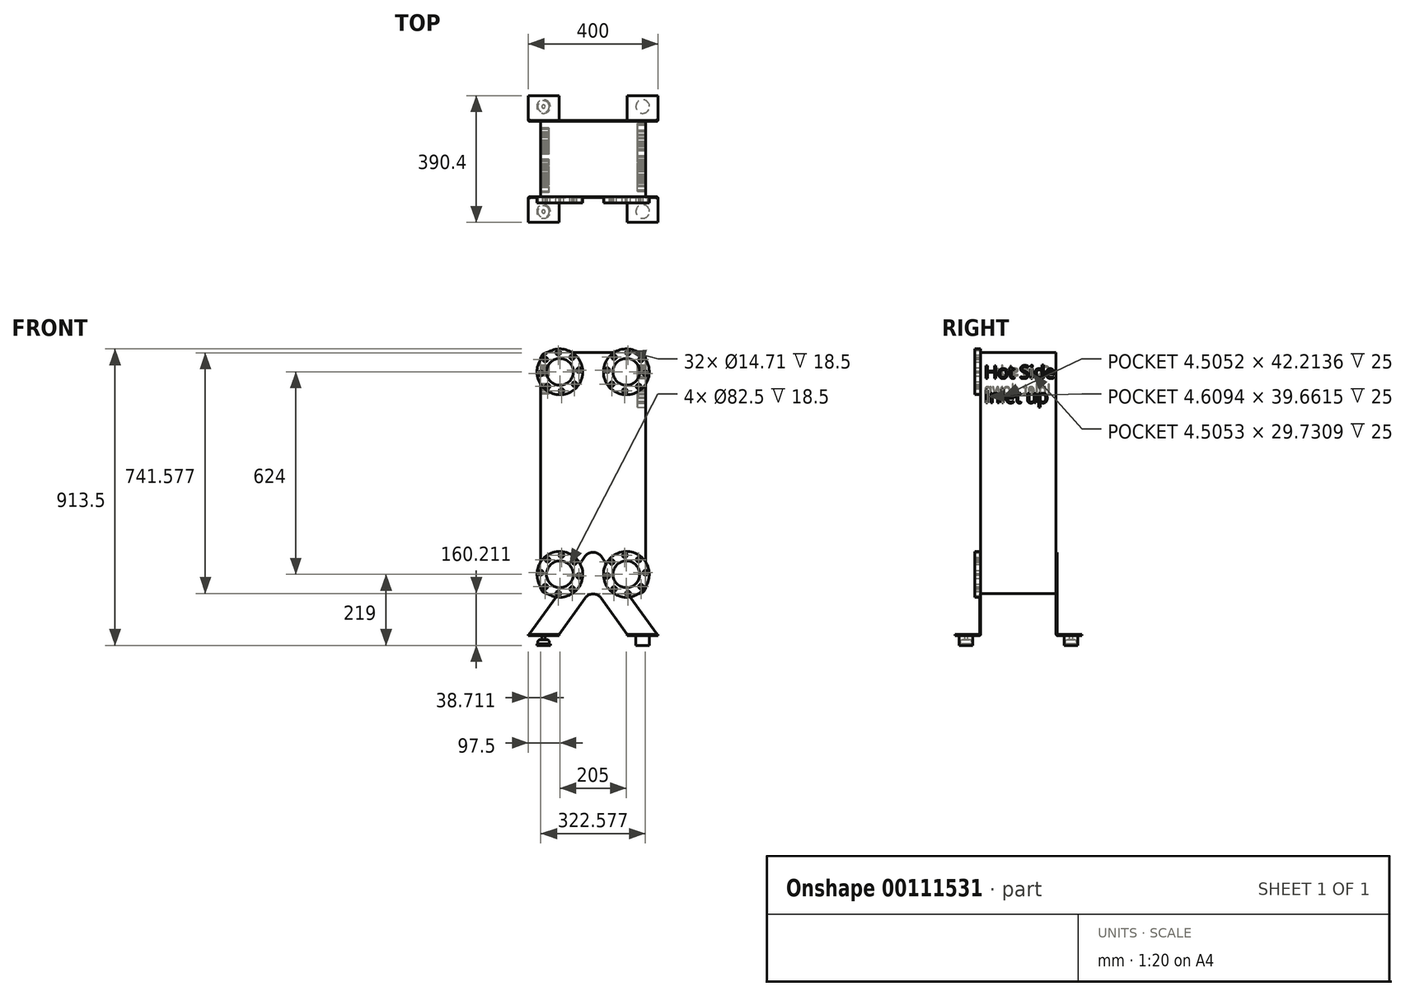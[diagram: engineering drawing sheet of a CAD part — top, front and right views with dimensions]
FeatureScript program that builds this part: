
annotation { "Feature Type Name" : "Feature", "Feature Type Description" : "" }
export const myFeature = defineFeature(function(context is Context, id is Id, definition is map)
    precondition{}
    {
        {
            var Q0;
            Q0=qCreatedBy(makeId("Front.planeOp"),FACE);
            var sketch = newSketch(context, id + "F0", { "sketchPlane" : qUnion([Q0])});
            skLineSegment(sketch, "E0.bottom", {"start": v(20, 0) * mm, "end": v(304, 0) * mm});
            skLineSegment(sketch, "E0.top", {"start": v(20, 742) * mm, "end": v(304, 742) * mm});
            skLineSegment(sketch, "E0.left", {"start": v(0, 20) * mm, "end": v(0, 722) * mm});
            skLineSegment(sketch, "E0.right", {"start": v(324, 20) * mm, "end": v(324, 722) * mm});
            skPoint(sketch, "E1", {"position": v(59.5, 683) * mm});
            skPoint(sketch, "E2", {"position": v(264.5, 683) * mm});
            skPoint(sketch, "E3", {"position": v(59.5, 59) * mm});
            skPoint(sketch, "E4", {"position": v(264.5, 59) * mm});
            skPoint(sketch, "E5", {"position": v(162, 0) * mm});
            skPoint(sketch, "E6", {"position": v(324, 371) * mm});
            skLineSegment(sketch, "E7", {"start": v(162, -155.7) * mm, "end": v(162, 967.26) * mm, "construction": true});
            skLineSegment(sketch, "E8", {"start": v(459.95, 371) * mm, "end": v(-440.95, 371) * mm, "construction": true});
            skLineSegment(sketch, "E9", {"start": v(59.5, 683) * mm, "end": v(162, 683) * mm});
            skLineSegment(sketch, "E10", {"start": v(162, 683) * mm, "end": v(264.5, 683) * mm});
            skLineSegment(sketch, "E11", {"start": v(59.5, 683) * mm, "end": v(59.5, 371) * mm});
            skLineSegment(sketch, "E12", {"start": v(59.5, 371) * mm, "end": v(59.5, 59) * mm});
            skPoint(sketch, "E13.visualSharp", {"position": v(0, 742) * mm});
            skArc(sketch, "E13.filletArc", {"start": v(20, 742) * mm, "mid": v(5.86, 736.14) * mm, "end": v(0, 722) * mm});
            skPoint(sketch, "E14.visualSharp", {"position": v(324, 742) * mm});
            skArc(sketch, "E14.filletArc", {"start": v(324, 722) * mm, "mid": v(318.14, 736.14) * mm, "end": v(304, 742) * mm});
            skPoint(sketch, "E15.visualSharp", {"position": v(324, 0) * mm});
            skArc(sketch, "E15.filletArc", {"start": v(304, 0) * mm, "mid": v(318.14, 5.86) * mm, "end": v(324, 20) * mm});
            skPoint(sketch, "E16.visualSharp", {"position": v(0, 0) * mm});
            skArc(sketch, "E16.filletArc", {"start": v(0, 20) * mm, "mid": v(5.86, 5.86) * mm, "end": v(20, 0) * mm});
            skSolve(sketch);
        }
        {
            var Q0;
            Q0=qSketchRegion(id+"F0",true);
            extrude(context, id + "F1", {"entities" : qUnion([Q0]), "oppositeDirection" : true, "depth" : 232.4 * mm});
        }
        {
            var Q0;
            Q0=makeQuery(id+"F0.imprint","IMPRINT",FACE,{"disambiguationData":[TD([[makeQuery(id+"F0.imprint","IMPRINT",EDGE,{"derivedFrom":sQuery(id+"F0.wireOp",EDGE,"E0.bottom")}),1.0]])]});
            var sketch = newSketch(context, id + "F2", { "sketchPlane" : qUnion([Q0])});
            skPoint(sketch, "E17.0", {"position": v(59.5, 683) * mm});
            skCircle(sketch, "E18", {"center": v(59.5, 683) * mm, "radius": 41.25 * mm});
            skCircle(sketch, "E19", {"center": v(59.5, 683) * mm, "radius": 70.5 * mm});
            skCircle(sketch, "E20", {"center": v(59.5, 683) * mm, "radius": 59 * mm, "construction": true});
            skCircle(sketch, "E21", {"center": v(21.46, 637.9) * mm, "radius": 7.35 * mm});
            skCircle(sketch, "E22.1.0", {"center": v(0.71, 678) * mm, "radius": 7.35 * mm});
            skCircle(sketch, "E22.2.0", {"center": v(14.4, 721.04) * mm, "radius": 7.35 * mm});
            skCircle(sketch, "E22.3.0", {"center": v(54.5, 741.79) * mm, "radius": 7.35 * mm});
            skCircle(sketch, "E22.4.0", {"center": v(97.54, 728.1) * mm, "radius": 7.35 * mm});
            skCircle(sketch, "E22.5.0", {"center": v(118.29, 688) * mm, "radius": 7.35 * mm});
            skCircle(sketch, "E22.6.0", {"center": v(104.6, 644.96) * mm, "radius": 7.35 * mm});
            skCircle(sketch, "E22.7.0", {"center": v(64.5, 624.21) * mm, "radius": 7.35 * mm});
            skLineSegment(sketch, "E22.anchor1", {"start": v(59.5, 683) * mm, "end": v(21.46, 637.9) * mm, "construction": true});
            skLineSegment(sketch, "E22.anchor2", {"start": v(59.5, 683) * mm, "end": v(64.5, 624.21) * mm, "construction": true});
            skPoint(sketch, "E23.0.MirrorP", {"position": v(264.5, 683) * mm});
            skCircle(sketch, "E23.1.MirrorC", {"center": v(226.46, 728.1) * mm, "radius": 7.35 * mm});
            skCircle(sketch, "E23.2.MirrorC", {"center": v(205.71, 688) * mm, "radius": 7.35 * mm});
            skCircle(sketch, "E23.3.MirrorC", {"center": v(219.4, 644.96) * mm, "radius": 7.35 * mm});
            skCircle(sketch, "E23.4.MirrorC", {"center": v(259.5, 624.21) * mm, "radius": 7.35 * mm});
            skLineSegment(sketch, "E23.5.MirrorCS", {"start": v(264.5, 683) * mm, "end": v(302.54, 637.9) * mm, "construction": true});
            skLineSegment(sketch, "E23.6.MirrorCS", {"start": v(264.5, 683) * mm, "end": v(259.5, 624.21) * mm, "construction": true});
            skCircle(sketch, "E23.7.MirrorC", {"center": v(269.5, 741.79) * mm, "radius": 7.35 * mm});
            skPoint(sketch, "E23.8.MirrorP", {"position": v(264.5, 683) * mm});
            skCircle(sketch, "E23.9.MirrorC", {"center": v(309.6, 721.04) * mm, "radius": 7.35 * mm});
            skCircle(sketch, "E23.10.MirrorC", {"center": v(264.5, 683) * mm, "radius": 59 * mm, "construction": true});
            skCircle(sketch, "E23.11.MirrorC", {"center": v(264.5, 683) * mm, "radius": 41.25 * mm});
            skCircle(sketch, "E23.12.MirrorC", {"center": v(264.5, 683) * mm, "radius": 70.5 * mm});
            skCircle(sketch, "E23.13.MirrorC", {"center": v(302.54, 637.9) * mm, "radius": 7.35 * mm});
            skCircle(sketch, "E23.14.MirrorC", {"center": v(323.29, 678) * mm, "radius": 7.35 * mm});
            skCircle(sketch, "E24.0.MirrorC", {"center": v(259.5, 117.79) * mm, "radius": 7.35 * mm});
            skCircle(sketch, "E24.1.MirrorC", {"center": v(21.46, 104.1) * mm, "radius": 7.35 * mm});
            skCircle(sketch, "E24.2.MirrorC", {"center": v(302.54, 104.1) * mm, "radius": 7.35 * mm});
            skPoint(sketch, "E24.3.MirrorP", {"position": v(264.5, 59) * mm});
            skCircle(sketch, "E24.4.MirrorC", {"center": v(14.4, 20.96) * mm, "radius": 7.35 * mm});
            skCircle(sketch, "E24.5.MirrorC", {"center": v(309.6, 20.96) * mm, "radius": 7.35 * mm});
            skCircle(sketch, "E24.6.MirrorC", {"center": v(219.4, 97.04) * mm, "radius": 7.35 * mm});
            skCircle(sketch, "E24.7.MirrorC", {"center": v(104.6, 97.04) * mm, "radius": 7.35 * mm});
            skCircle(sketch, "E24.8.MirrorC", {"center": v(118.29, 54) * mm, "radius": 7.35 * mm});
            skCircle(sketch, "E24.9.MirrorC", {"center": v(97.54, 13.9) * mm, "radius": 7.35 * mm});
            skCircle(sketch, "E24.10.MirrorC", {"center": v(269.5, 0.21) * mm, "radius": 7.35 * mm});
            skCircle(sketch, "E24.11.MirrorC", {"center": v(226.46, 13.9) * mm, "radius": 7.35 * mm});
            skCircle(sketch, "E24.12.MirrorC", {"center": v(205.71, 54) * mm, "radius": 7.35 * mm});
            skPoint(sketch, "E24.13.MirrorP", {"position": v(59.5, 59) * mm});
            skPoint(sketch, "E24.14.MirrorP", {"position": v(264.5, 59) * mm});
            skLineSegment(sketch, "E24.15.MirrorCS", {"start": v(264.5, 59) * mm, "end": v(302.54, 104.1) * mm, "construction": true});
            skCircle(sketch, "E24.16.MirrorC", {"center": v(264.5, 59) * mm, "radius": 59 * mm, "construction": true});
            skCircle(sketch, "E24.17.MirrorC", {"center": v(54.5, 0.21) * mm, "radius": 7.35 * mm});
            skCircle(sketch, "E24.18.MirrorC", {"center": v(0.71, 64) * mm, "radius": 7.35 * mm});
            skCircle(sketch, "E24.19.MirrorC", {"center": v(59.5, 59) * mm, "radius": 59 * mm, "construction": true});
            skCircle(sketch, "E24.20.MirrorC", {"center": v(264.5, 59) * mm, "radius": 70.5 * mm});
            skCircle(sketch, "E24.21.MirrorC", {"center": v(59.5, 59) * mm, "radius": 70.5 * mm});
            skCircle(sketch, "E24.22.MirrorC", {"center": v(59.5, 59) * mm, "radius": 41.25 * mm});
            skPoint(sketch, "E24.23.MirrorP", {"position": v(59.5, 59) * mm});
            skCircle(sketch, "E24.24.MirrorC", {"center": v(264.5, 59) * mm, "radius": 41.25 * mm});
            skCircle(sketch, "E24.25.MirrorC", {"center": v(323.29, 64) * mm, "radius": 7.35 * mm});
            skCircle(sketch, "E24.26.MirrorC", {"center": v(64.5, 117.79) * mm, "radius": 7.35 * mm});
            skLineSegment(sketch, "E24.27.MirrorCS", {"start": v(264.5, 59) * mm, "end": v(259.5, 117.79) * mm, "construction": true});
            skLineSegment(sketch, "E24.28.MirrorCS", {"start": v(59.5, 59) * mm, "end": v(21.46, 104.1) * mm, "construction": true});
            skLineSegment(sketch, "E24.29.MirrorCS", {"start": v(59.5, 59) * mm, "end": v(64.5, 117.79) * mm, "construction": true});
            skSolve(sketch);
        }
        {
            var Q0;
            Q0=qSketchRegion(id+"F2",true);
            extrude(context, id + "F3", {"entities" : qUnion([Q0]), "operationType" : NewBodyOperationType.ADD, "depth" : 18.5 * mm});
        }
        {
            var Q0;
            Q0=makeQuery(id+"F0.imprint","IMPRINT",FACE,{"disambiguationData":[TD([[makeQuery(id+"F0.imprint","IMPRINT",EDGE,{"derivedFrom":sQuery(id+"F0.wireOp",EDGE,"E0.bottom")}),1.0]])]});
            var sketch = newSketch(context, id + "F4", { "sketchPlane" : qUnion([Q0])});
            skLineSegment(sketch, "E25", {"start": v(-108.27, -130) * mm, "end": v(594.7, -130) * mm, "construction": true});
            skLineSegment(sketch, "E26.0", {"start": v(162, -155.7) * mm, "end": v(162, 967.26) * mm});
            skPoint(sketch, "E27", {"position": v(162, -130) * mm});
            skLineSegment(sketch, "E28", {"start": v(137.63, 114.63) * mm, "end": v(121.62, 92.33) * mm});
            skLineSegment(sketch, "E29.0.MirrorCS", {"start": v(186.37, 114.63) * mm, "end": v(202.38, 92.33) * mm});
            skPoint(sketch, "E30.visualSharp", {"position": v(162, 148.58) * mm});
            skArc(sketch, "E30.filletArc", {"start": v(186.37, 114.63) * mm, "mid": v(162, 127.14) * mm, "end": v(137.63, 114.63) * mm});
            skLineSegment(sketch, "E31.0", {"start": v(137.63, -13.97) * mm, "end": v(54.33, -130) * mm});
            skLineSegment(sketch, "E31.1", {"start": v(186.37, -13.97) * mm, "end": v(269.67, -130) * mm});
            skLineSegment(sketch, "E32", {"start": v(-38, -130) * mm, "end": v(54.33, -130) * mm});
            skLineSegment(sketch, "E33", {"start": v(269.67, -130) * mm, "end": v(362, -130) * mm});
            skPoint(sketch, "E34.visualSharp", {"position": v(162, 19.98) * mm});
            skArc(sketch, "E34.filletArc", {"start": v(186.37, -13.97) * mm, "mid": v(162, -1.46) * mm, "end": v(137.63, -13.97) * mm});
            skArc(sketch, "E35.0", {"start": v(47.78, -10.52) * mm, "mid": v(116.77, 17.88) * mm, "end": v(121.62, 92.33) * mm});
            skArc(sketch, "E36.0", {"start": v(202.38, 92.33) * mm, "mid": v(207.23, 17.88) * mm, "end": v(276.22, -10.52) * mm});
            skLineSegment(sketch, "E37.trimOffspring", {"start": v(47.78, -10.52) * mm, "end": v(-38, -130) * mm});
            skLineSegment(sketch, "E38.trimOffspring", {"start": v(276.22, -10.52) * mm, "end": v(362, -130) * mm});
            skSolve(sketch);
        }
        {
            var Q0;
            Q0=qSketchRegion(id+"F4",true);
            extrude(context, id + "F5", {"entities" : qUnion([Q0]), "depth" : 3 * mm});
        }
        {
            var Q0;
            Q0=makeQuery(id+"F5.opExtrude","CAP_FACE",FACE,{"disambiguationData":[OSD([sQuery(id+"F4.wireOp",EDGE,"E28"),sQuery(id+"F4.wireOp",EDGE,"E29.0.MirrorCS"),sQuery(id+"F4.wireOp",EDGE,"E30.filletArc"),sQuery(id+"F4.wireOp",EDGE,"E31.0"),sQuery(id+"F4.wireOp",EDGE,"E31.1"),sQuery(id+"F4.wireOp",EDGE,"E32"),sQuery(id+"F4.wireOp",EDGE,"E33"),sQuery(id+"F4.wireOp",EDGE,"E34.filletArc"),sQuery(id+"F4.wireOp",EDGE,"E35.0"),sQuery(id+"F4.wireOp",EDGE,"E36.0"),sQuery(id+"F4.wireOp",EDGE,"E37.trimOffspring"),sQuery(id+"F4.wireOp",EDGE,"E38.trimOffspring")])],"isStart":false});
            var sketch = newSketch(context, id + "F6", { "sketchPlane" : qUnion([Q0])});
            skLineSegment(sketch, "E39.0", {"start": v(-38, -130) * mm, "end": v(54.33, -130) * mm});
            skLineSegment(sketch, "E40.bottom", {"start": v(-38, -130) * mm, "end": v(57.2, -130) * mm});
            skLineSegment(sketch, "E40.top", {"start": v(-38, -126) * mm, "end": v(57.2, -126) * mm});
            skLineSegment(sketch, "E40.left", {"start": v(-38, -130) * mm, "end": v(-38, -126) * mm});
            skLineSegment(sketch, "E40.right", {"start": v(57.2, -130) * mm, "end": v(57.2, -126) * mm});
            skLineSegment(sketch, "E41.0.MirrorCS", {"start": v(362, -130) * mm, "end": v(266.8, -130) * mm});
            skLineSegment(sketch, "E41.1.MirrorCS", {"start": v(362, -126) * mm, "end": v(266.8, -126) * mm});
            skLineSegment(sketch, "E41.2.MirrorCS", {"start": v(266.8, -130) * mm, "end": v(266.8, -126) * mm});
            skLineSegment(sketch, "E41.3.MirrorCS", {"start": v(362, -130) * mm, "end": v(362, -126) * mm});
            skLineSegment(sketch, "E41.4.MirrorCS", {"start": v(362, -130) * mm, "end": v(269.67, -130) * mm});
            skSolve(sketch);
        }
        {
            var Q0;
            Q0=qSketchRegion(id+"F6",true);
            extrude(context, id + "F7", {"entities" : qUnion([Q0]), "operationType" : NewBodyOperationType.ADD, "depth" : 76 * mm});
        }
        {
            var Q0;
            {var subQ0=sQuery(id+"F6.wireOp",EDGE,"E40.top");var subQ3=sQuery(id+"F4.wireOp",EDGE,"E31.0");Q0=makeQuery(id+"F7.boolean.opBoolean","SPLIT",EDGE,{"disambiguationData":[TD([makeQuery(id+"F5.opExtrude","SWEPT_FACE",FACE,{"disambiguationData":[OSD([subQ3])]})])],"derivedFrom":makeQuery(id+"F7.opExtrude","CAP_EDGE",EDGE,{"disambiguationData":[OSD([subQ0])],"isStart":true})});}
            var Q1;
            {var subQ0=sQuery(id+"F6.wireOp",EDGE,"E41.1.MirrorCS");var subQ3=sQuery(id+"F4.wireOp",EDGE,"E31.1");Q1=makeQuery(id+"F7.boolean.opBoolean","SPLIT",EDGE,{"disambiguationData":[TD([makeQuery(id+"F5.opExtrude","SWEPT_FACE",FACE,{"disambiguationData":[OSD([subQ3])]})])],"derivedFrom":makeQuery(id+"F7.opExtrude","CAP_EDGE",EDGE,{"disambiguationData":[OSD([subQ0])],"isStart":true})});}
            var Q2;
            Q2=makeQuery(id+"F5.opExtrude","CAP_EDGE",EDGE,{"disambiguationData":[OSD([sQuery(id+"F4.wireOp",EDGE,"E33")])],"isStart":true});
            var Q3;
            Q3=makeQuery(id+"F5.opExtrude","CAP_EDGE",EDGE,{"disambiguationData":[OSD([sQuery(id+"F4.wireOp",EDGE,"E32")])],"isStart":true});
            fillet(context, id + "F8", {"entities" : qUnion([Q0, Q1, Q2, Q3]), "radius" : 5 * mm, "tangentPropagation" : true, "allowEdgeOverflow" : false});
        }
        {
            var Q0;
            Q0=makeQuery(id+"F7.boolean.opBoolean","MERGE",FACE,{"derivedFrom":[makeQuery(id+"F5.opExtrude","SWEPT_FACE",FACE,{"disambiguationData":[OSD([sQuery(id+"F4.wireOp",EDGE,"E33")])]}),makeQuery(id+"F7.opExtrude","SWEPT_FACE",FACE,{"disambiguationData":[OSD([sQuery(id+"F6.wireOp",EDGE,"E41.0.MirrorCS"),sQuery(id+"F6.wireOp",EDGE,"E41.4.MirrorCS")])]})]});
            var sketch = newSketch(context, id + "F9", { "sketchPlane" : qUnion([Q0])});
            skCircle(sketch, "E42", {"center": v(9.19, 45.56) * mm, "radius": 20.99 * mm});
            skPoint(sketch, "E43.0", {"position": v(162, 0) * mm});
            skLineSegment(sketch, "E44", {"start": v(162, -5.76) * mm, "end": v(162, 57.48) * mm, "construction": true});
            skCircle(sketch, "E45.0.MirrorC", {"center": v(314.81, 45.56) * mm, "radius": 20.99 * mm});
            skSolve(sketch);
        }
        {
            var Q0;
            Q0=qSketchRegion(id+"F9",true);
            extrude(context, id + "F10", {"entities" : qUnion([Q0]), "operationType" : NewBodyOperationType.ADD, "depth" : 30 * mm});
        }
        {
            var Q0;
            Q0=sQuery(id+"F9.wireOp",VERTEX,"E42.center");
            var Q1;
            Q1=qCreatedBy(makeId("Front.planeOp"),FACE);
            cPlane(context, id + "F11", {"entities" : qUnion([Q0, Q1]), "cplaneType" : CPlaneType.PLANE_POINT, "offset" : 150 * mm, "width" : 150 * mm, "height" : 150 * mm});
        }
        {
            var Q0;
            Q0=qCreatedBy(id+"F11.planeOp",FACE);
            var sketch = newSketch(context, id + "F12", { "sketchPlane" : qUnion([Q0])});
            skLineSegment(sketch, "E46.1", {"start": v(14.22, -130) * mm, "end": v(57.2, -130) * mm});
            skLineSegment(sketch, "E47", {"start": v(30.17, -130) * mm, "end": v(30.17, -155.75) * mm});
            skPoint(sketch, "E48.0", {"position": v(9.19, -130) * mm});
            skLineSegment(sketch, "E49", {"start": v(9.19, -108.08) * mm, "end": v(9.19, -184.47) * mm, "construction": true});
            skLineSegment(sketch, "E50", {"start": v(14.22, -130) * mm, "end": v(14.22, -142.48) * mm});
            skLineSegment(sketch, "E51", {"start": v(14.22, -142.48) * mm, "end": v(19.9, -142.48) * mm});
            skLineSegment(sketch, "E52", {"start": v(26.9, -149.48) * mm, "end": v(26.9, -155.75) * mm});
            skLineSegment(sketch, "E53", {"start": v(26.9, -155.75) * mm, "end": v(30.17, -155.75) * mm});
            skPoint(sketch, "E54.visualSharp", {"position": v(26.9, -142.48) * mm});
            skArc(sketch, "E54.filletArc", {"start": v(26.9, -149.48) * mm, "mid": v(24.86, -144.53) * mm, "end": v(19.9, -142.48) * mm});
            skLineSegment(sketch, "E55", {"start": v(14.22, -130) * mm, "end": v(30.17, -130) * mm});
            skPoint(sketch, "E56.0.end.orphan", {"position": v(-11.8, -160) * mm});
            skPoint(sketch, "E57.end.orphan", {"position": v(30.17, -160) * mm});
            skPoint(sketch, "E57.start.orphan", {"position": v(9.19, -160) * mm});
            skPoint(sketch, "E58.orphan", {"position": v(-38, -130) * mm});
            skSolve(sketch);
        }
        {
            var Q0;
            Q0=qSketchRegion(id+"F12",true);
            var Q1;
            Q1=sQuery(id+"F12.wireOp",EDGE,"E49");
            revolve(context, id + "F13", {"operationType" : NewBodyOperationType.REMOVE, "entities" : qUnion([Q0]), "axis" : qUnion([Q1]), "revolveType" : RevolveType.FULL, "oppositeDirection" : true});
        }
        {
            var Q0;
            Q0=qCreatedBy(makeId("Front.planeOp"),FACE);
            cPlane(context, id + "F14", {"entities" : qUnion([Q0]), "cplaneType" : CPlaneType.OFFSET, "offset" : 116.2 * mm, "oppositeDirection" : true, "width" : 150 * mm, "height" : 150 * mm});
        }
        {
            var Q0;
            Q0=makeQuery(id+"F5.opExtrude","SWEPT_BODY",BODY,{"disambiguationData":[OSD([sQuery(id+"F4.wireOp",EDGE,"E28"),sQuery(id+"F4.wireOp",EDGE,"E29.0.MirrorCS"),sQuery(id+"F4.wireOp",EDGE,"E30.filletArc"),sQuery(id+"F4.wireOp",EDGE,"E31.0"),sQuery(id+"F4.wireOp",EDGE,"E31.1"),sQuery(id+"F4.wireOp",EDGE,"E32"),sQuery(id+"F4.wireOp",EDGE,"E33"),sQuery(id+"F4.wireOp",EDGE,"E34.filletArc"),sQuery(id+"F4.wireOp",EDGE,"E35.0"),sQuery(id+"F4.wireOp",EDGE,"E36.0"),sQuery(id+"F4.wireOp",EDGE,"E37.trimOffspring"),sQuery(id+"F4.wireOp",EDGE,"E38.trimOffspring")])]});
            var Q1;
            Q1=qCreatedBy(id+"F14.planeOp",FACE);
            mirror(context, id + "F15", {"operationType" : NewBodyOperationType.ADD, "entities" : qUnion([Q0]), "mirrorPlane" : qUnion([Q1])});
        }
        {
            var Q0;
            Q0=makeQuery(id+"F1.opExtrude","SWEPT_FACE",FACE,{"disambiguationData":[OSD([sQuery(id+"F0.wireOp",EDGE,"E0.right")])]});
            var sketch = newSketch(context, id + "F16", { "sketchPlane" : qUnion([Q0])});
            skText(sketch, "E59", { "text": "Hot Side\nInlet up", "fontName": "OpenSans-Regular.ttf"});
            const initialGuessF16  = {"E59": [0.01105, 0.66274, 1, 0, 0.04]};
            skSetInitialGuess(sketch, initialGuessF16);
            skSolve(sketch);
        }
        {
            var Q0;
            Q0=qSketchRegion(id+"F16",true);
            extrude(context, id + "F17", {"entities" : qUnion([Q0]), "operationType" : NewBodyOperationType.REMOVE, "oppositeDirection" : true, "depth" : 25 * mm});
        }
        {
            var Q0;
            Q0=makeQuery(id+"F1.opExtrude","SWEPT_FACE",FACE,{"disambiguationData":[OSD([sQuery(id+"F0.wireOp",EDGE,"E0.left")])]});
            var sketch = newSketch(context, id + "F18", { "sketchPlane" : qUnion([Q0])});
            skText(sketch, "E60", { "text": "Cold side\nInlet down", "fontName": "OpenSans-Regular.ttf"});
            const initialGuessF18  = {"E60": [-0.21529, 0.67114, 1, 0, 0.03]};
            skSetInitialGuess(sketch, initialGuessF18);
            skSolve(sketch);
        }
        {
            var Q0;
            Q0=qSketchRegion(id+"F18",true);
            extrude(context, id + "F19", {"entities" : qUnion([Q0]), "operationType" : NewBodyOperationType.REMOVE, "oppositeDirection" : true, "depth" : 25 * mm});
        }
    });
